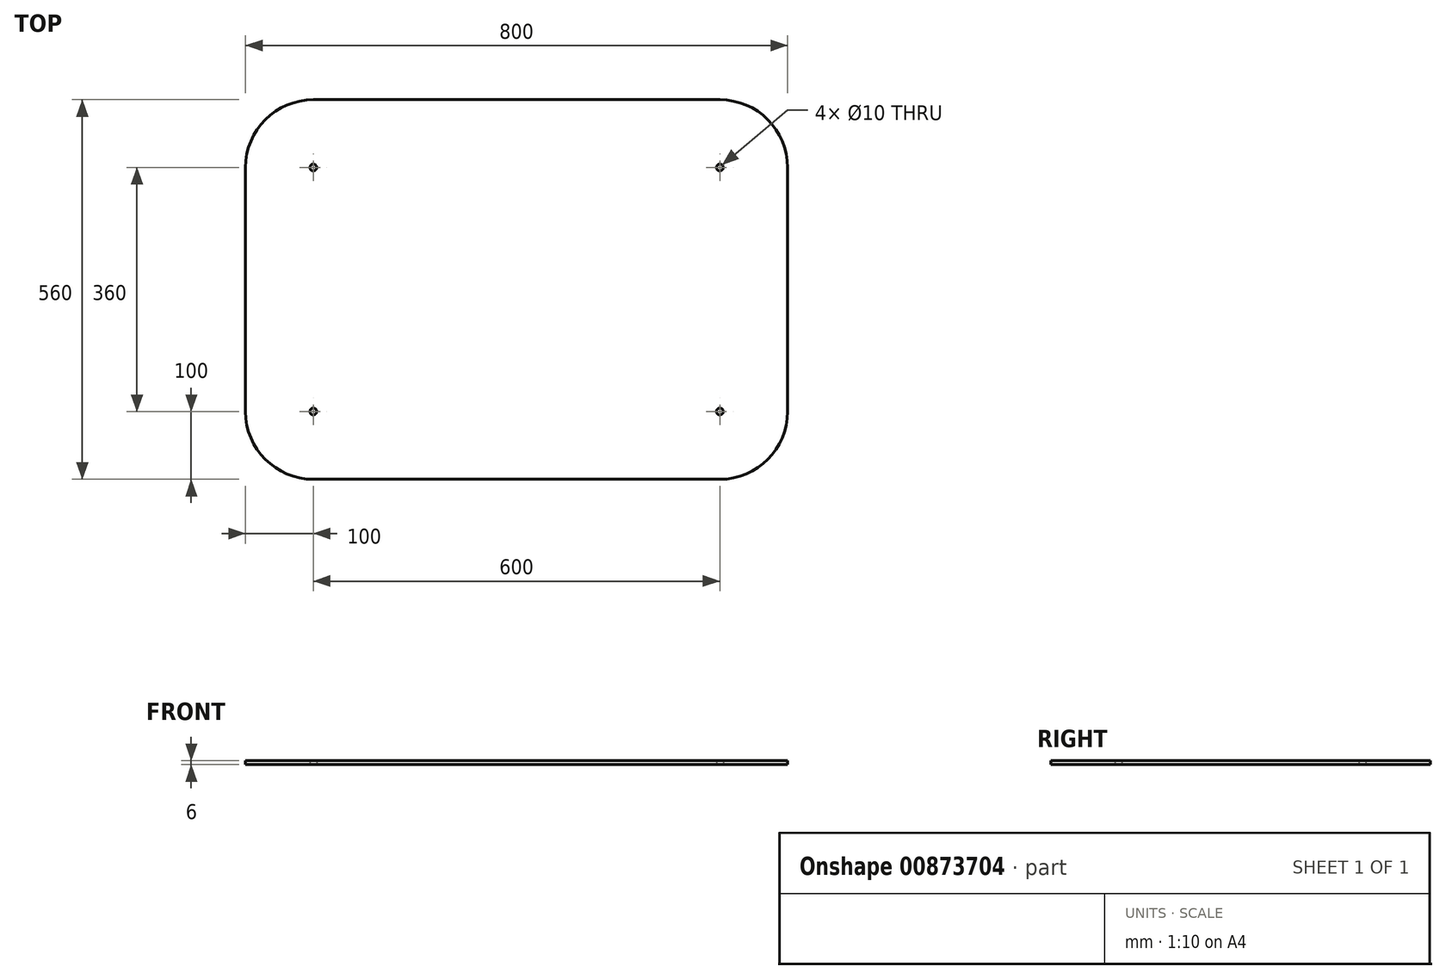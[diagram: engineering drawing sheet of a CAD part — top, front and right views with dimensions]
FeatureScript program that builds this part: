
annotation { "Feature Type Name" : "Feature", "Feature Type Description" : "" }
export const myFeature = defineFeature(function(context is Context, id is Id, definition is map)
    precondition{}
    {
        {
            var Q0;
            Q0=qCreatedBy(makeId("Top.planeOp"),FACE);
            var sketch = newSketch(context, id + "F0", { "sketchPlane" : qUnion([Q0])});
            skLineSegment(sketch, "E0.bottom", {"start": v(300, -280) * mm, "end": v(-300, -280) * mm});
            skLineSegment(sketch, "E0.top", {"start": v(300, 280) * mm, "end": v(-300, 280) * mm});
            skLineSegment(sketch, "E0.left", {"start": v(400, -180) * mm, "end": v(400, 180) * mm});
            skLineSegment(sketch, "E0.right", {"start": v(-400, -180) * mm, "end": v(-400, 180) * mm});
            skPoint(sketch, "E0.middle", {"position": v(0, 0) * mm});
            skPoint(sketch, "E1.visualSharp", {"position": v(400, 280) * mm});
            skArc(sketch, "E1.filletArc", {"start": v(400, 180) * mm, "mid": v(370.71, 250.71) * mm, "end": v(300, 280) * mm});
            skPoint(sketch, "E2.visualSharp", {"position": v(400, -280) * mm});
            skArc(sketch, "E2.filletArc", {"start": v(300, -280) * mm, "mid": v(370.71, -250.71) * mm, "end": v(400, -180) * mm});
            skPoint(sketch, "E3.visualSharp", {"position": v(-400, -280) * mm});
            skArc(sketch, "E3.filletArc", {"start": v(-400, -180) * mm, "mid": v(-370.71, -250.71) * mm, "end": v(-300, -280) * mm});
            skPoint(sketch, "E4.visualSharp", {"position": v(-400, 280) * mm});
            skArc(sketch, "E4.filletArc", {"start": v(-300, 280) * mm, "mid": v(-370.71, 250.71) * mm, "end": v(-400, 180) * mm});
            skCircle(sketch, "E5", {"center": v(-300, 180) * mm, "radius": 5 * mm});
            skCircle(sketch, "E6", {"center": v(-300, -180) * mm, "radius": 5 * mm});
            skCircle(sketch, "E7", {"center": v(300, 180) * mm, "radius": 5 * mm});
            skCircle(sketch, "E8", {"center": v(300, -180) * mm, "radius": 5 * mm});
            skSolve(sketch);
        }
        {
            var Q0;
            Q0=makeQuery(id+"F0.imprint","IMPRINT",FACE,{"disambiguationData":[TD([[makeQuery(id+"F0.imprint","IMPRINT",EDGE,{"derivedFrom":sQuery(id+"F0.wireOp",EDGE,"E0.bottom")}),-1.0]])]});
            extrude(context, id + "F1", {"entities" : qUnion([Q0]), "depth" : 6 * mm, "offsetDistance" : 25 * mm});
        }
    });
